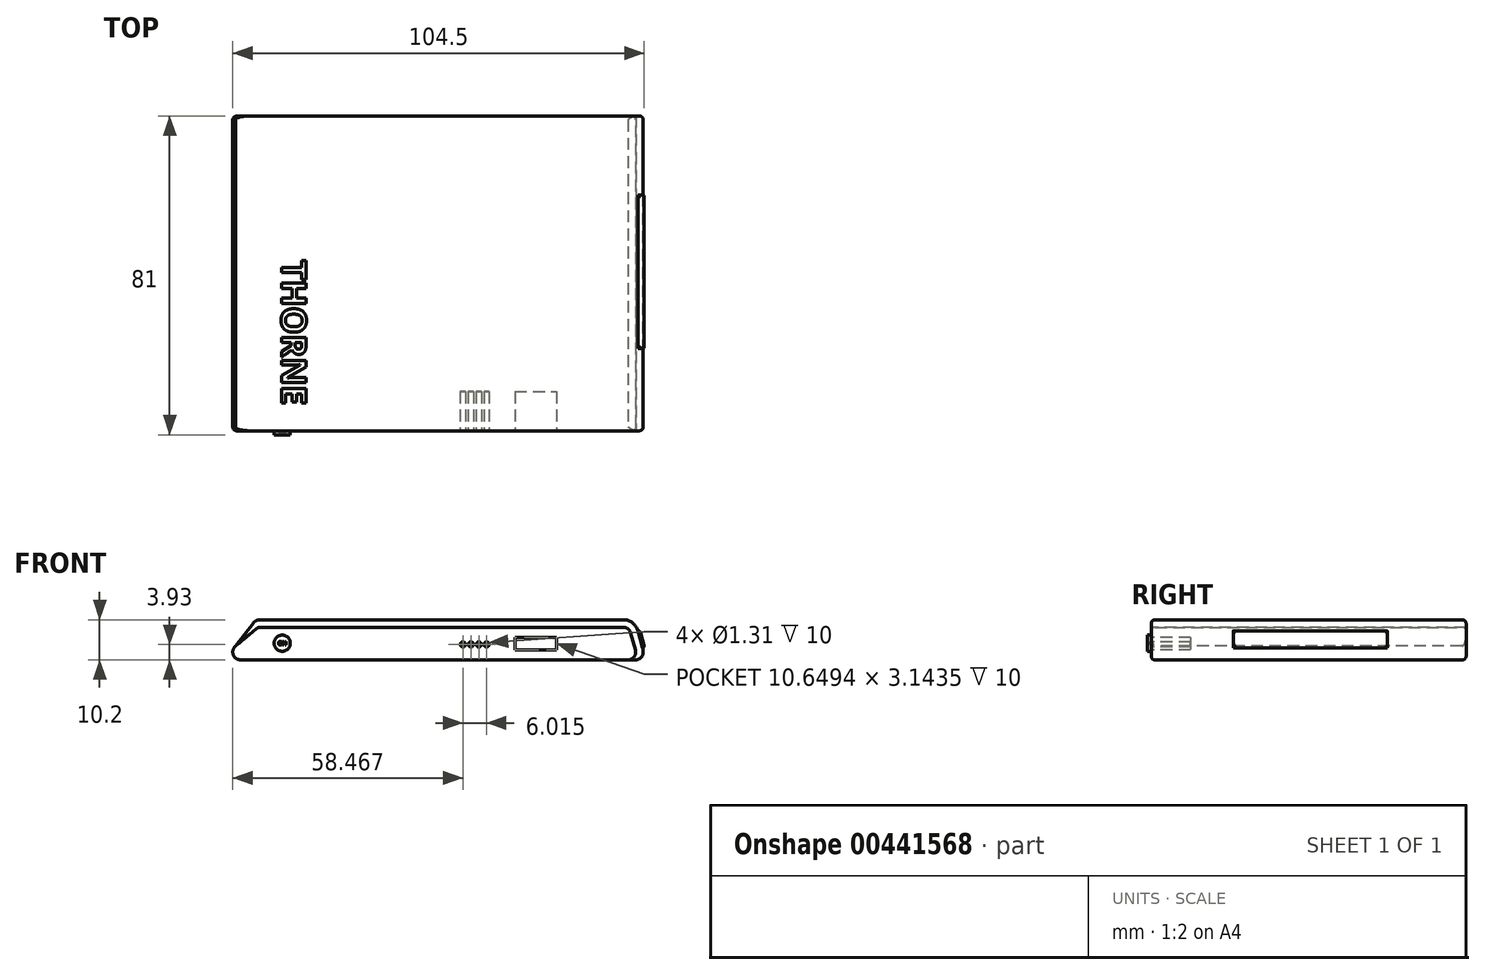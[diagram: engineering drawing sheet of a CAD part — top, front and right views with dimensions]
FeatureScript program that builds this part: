
annotation { "Feature Type Name" : "Feature", "Feature Type Description" : "" }
export const myFeature = defineFeature(function(context is Context, id is Id, definition is map)
    precondition{}
    {
        {
            var Q0;
            Q0=qCreatedBy(makeId("Front.planeOp"),FACE);
            var sketch = newSketch(context, id + "F0", { "sketchPlane" : qUnion([Q0])});
            skLineSegment(sketch, "E0", {"start": v(-44.25, -33) * mm, "end": v(54.14, -33) * mm});
            skFitSpline(sketch, "E1", {"points": [v(-49.78, -33) * mm, v(-39.82, -24.7) * mm], "startDerivative": vector(9.96, 8.3) * mm, "endDerivative": vector(9.96, 8.3) * mm});
            skLineSegment(sketch, "E2", {"start": v(-39.1, -24.7) * mm, "end": v(52.92, -24.7) * mm});
            skLineSegment(sketch, "E3", {"start": v(54.85, -26.16) * mm, "end": v(56.06, -30.46) * mm});
            skArc(sketch, "E4.filletArc", {"start": v(-39.1, -24.7) * mm, "mid": v(-39.78, -24.82) * mm, "end": v(-40.38, -25.17) * mm});
            skArc(sketch, "E5.filletArc", {"start": v(-45.53, -29.46) * mm, "mid": v(-46.13, -31.68) * mm, "end": v(-44.25, -33) * mm});
            skPoint(sketch, "E6.visualSharp", {"position": v(56.78, -33) * mm});
            skArc(sketch, "E6.filletArc", {"start": v(54.14, -33) * mm, "mid": v(55.73, -32.2) * mm, "end": v(56.06, -30.46) * mm});
            skPoint(sketch, "E7.visualSharp", {"position": v(54.44, -24.7) * mm});
            skArc(sketch, "E7.filletArc", {"start": v(54.85, -26.16) * mm, "mid": v(54.13, -25.1) * mm, "end": v(52.92, -24.7) * mm});
            skSolve(sketch);
        }
        {
            var Q0;
            Q0=makeQuery(id+"F0.imprint","IMPRINT",FACE,{"disambiguationData":[TD([[makeQuery(id+"F0.imprint","IMPRINT",EDGE,{"derivedFrom":sQuery(id+"F0.wireOp",EDGE,"E0")}),1.0]])]});
            extrude(context, id + "F1", {"entities" : qUnion([Q0]), "depth" : 80 * mm});
        }
        {
            var Q0;
            Q0=makeQuery(id+"F1.opExtrude","CAP_FACE",FACE,{"disambiguationData":[OSD([sQuery(id+"F0.wireOp",EDGE,"E0"),sQuery(id+"F0.wireOp",EDGE,"E1"),sQuery(id+"F0.wireOp",EDGE,"E2"),sQuery(id+"F0.wireOp",EDGE,"E3"),sQuery(id+"F0.wireOp",EDGE,"E4.filletArc"),sQuery(id+"F0.wireOp",EDGE,"E5.filletArc"),sQuery(id+"F0.wireOp",EDGE,"E6.filletArc"),sQuery(id+"F0.wireOp",EDGE,"E7.filletArc")])],"isStart":false});
            var sketch = newSketch(context, id + "F2", { "sketchPlane" : qUnion([Q0])});
            skCircle(sketch, "E8", {"center": v(18.23, -29.07) * mm, "radius": 0.66 * mm});
            skCircle(sketch, "E9", {"center": v(12.22, -29.07) * mm, "radius": 0.66 * mm});
            skCircle(sketch, "E10", {"center": v(16.26, -29.07) * mm, "radius": 0.66 * mm});
            skCircle(sketch, "E11", {"center": v(14.24, -29.07) * mm, "radius": 0.66 * mm});
            skLineSegment(sketch, "E12.bottom", {"start": v(25.42, -27.31) * mm, "end": v(36.07, -27.31) * mm});
            skLineSegment(sketch, "E12.top", {"start": v(25.42, -30.46) * mm, "end": v(36.07, -30.46) * mm});
            skLineSegment(sketch, "E12.left", {"start": v(25.42, -27.31) * mm, "end": v(25.42, -30.46) * mm});
            skLineSegment(sketch, "E12.right", {"start": v(36.07, -27.31) * mm, "end": v(36.07, -30.46) * mm});
            skSolve(sketch);
        }
        {
            var Q0;
            Q0 = qSketchRegion(id + "F2", true);
            extrude(context, id + "F3", {"entities" : qUnion([Q0]), "operationType" : NewBodyOperationType.REMOVE, "oppositeDirection" : true, "depth" : 10 * mm});
        }
        {
            var Q0;
            Q0=makeQuery(id+"F1.opExtrude","CAP_FACE",FACE,{"disambiguationData":[OSD([sQuery(id+"F0.wireOp",EDGE,"E0"),sQuery(id+"F0.wireOp",EDGE,"E1"),sQuery(id+"F0.wireOp",EDGE,"E2"),sQuery(id+"F0.wireOp",EDGE,"E3"),sQuery(id+"F0.wireOp",EDGE,"E4.filletArc"),sQuery(id+"F0.wireOp",EDGE,"E5.filletArc"),sQuery(id+"F0.wireOp",EDGE,"E6.filletArc"),sQuery(id+"F0.wireOp",EDGE,"E7.filletArc")])],"isStart":false});
            var sketch = newSketch(context, id + "F4", { "sketchPlane" : qUnion([Q0])});
            skCircle(sketch, "E13", {"center": v(-33.68, -28.76) * mm, "radius": 2.05 * mm});
            skSolve(sketch);
        }
        {
            var Q0;
            Q0=makeQuery(id+"F4.imprint","IMPRINT",FACE,{"disambiguationData":[TD([[makeQuery(id+"F4.imprint","IMPRINT",EDGE,{"derivedFrom":sQuery(id+"F4.wireOp",EDGE,"E13")}),1.0]])]});
            extrude(context, id + "F5", {"entities" : qUnion([Q0]), "operationType" : NewBodyOperationType.ADD, "depth" : 1 * mm});
        }
        {
            var Q0;
            Q0=makeQuery(id+"F5.opExtrude","CAP_FACE",FACE,{"disambiguationData":[OSD([sQuery(id+"F4.wireOp",EDGE,"E13")])],"isStart":false});
            var sketch = newSketch(context, id + "F6", { "sketchPlane" : qUnion([Q0])});
            skText(sketch, "E14", { "text": "ON", "fontName": "OpenSans-Bold.ttf"});
            const initialGuessF6  = {"E14": [-0.03474, -0.02925, 1, 0, 0.00097]};
            skSetInitialGuess(sketch, initialGuessF6);
            skSolve(sketch);
        }
        {
            var Q0;
            Q0 = qSketchRegion(id + "F6", true);
            extrude(context, id + "F7", {"entities" : qUnion([Q0]), "operationType" : NewBodyOperationType.REMOVE, "oppositeDirection" : true, "depth" : 0.3 * mm});
        }
        {
            var Q0;
            Q0=makeQuery(id+"F1.opExtrude","CAP_FACE",FACE,{"disambiguationData":[OSD([sQuery(id+"F0.wireOp",EDGE,"E0"),sQuery(id+"F0.wireOp",EDGE,"E1"),sQuery(id+"F0.wireOp",EDGE,"E2"),sQuery(id+"F0.wireOp",EDGE,"E3"),sQuery(id+"F0.wireOp",EDGE,"E4.filletArc"),sQuery(id+"F0.wireOp",EDGE,"E5.filletArc"),sQuery(id+"F0.wireOp",EDGE,"E6.filletArc"),sQuery(id+"F0.wireOp",EDGE,"E7.filletArc")])],"isStart":false});
            var sketch = newSketch(context, id + "F8", { "sketchPlane" : qUnion([Q0])});
            skLineSegment(sketch, "E15", {"start": v(54.14, -33) * mm, "end": v(56.04, -33) * mm});
            skArc(sketch, "E16.0", {"start": v(58.04, -31) * mm, "mid": v(58, -30.46) * mm, "end": v(57.9, -29.94) * mm});
            skLineSegment(sketch, "E16.1", {"start": v(56.68, -25.64) * mm, "end": v(57.9, -29.94) * mm});
            skArc(sketch, "E16.2", {"start": v(56.68, -25.64) * mm, "mid": v(55.28, -23.6) * mm, "end": v(52.92, -22.8) * mm});
            skPoint(sketch, "E17.visualSharp", {"position": v(57.49, -33) * mm});
            skArc(sketch, "E17.filletArc", {"start": v(56.04, -33) * mm, "mid": v(57.45, -32.41) * mm, "end": v(58.04, -31) * mm});
            skLineSegment(sketch, "E18", {"start": v(52.92, -22.8) * mm, "end": v(-39.4, -22.8) * mm});
            skLineSegment(sketch, "E19", {"start": v(-40.98, -23.58) * mm, "end": v(-45.53, -29.46) * mm});
            skPoint(sketch, "E20.endSnap0", {"position": v(-39.78, -24.82) * mm});
            skArc(sketch, "E21.0", {"start": v(54.14, -33) * mm, "mid": v(55.73, -32.2) * mm, "end": v(56.06, -30.46) * mm});
            skLineSegment(sketch, "E21.1", {"start": v(54.85, -26.16) * mm, "end": v(56.06, -30.46) * mm});
            skFitSpline(sketch, "E21.2", {"points": [v(-49.78, -33) * mm, v(-46.46, -30.23) * mm, v(-43.14, -27.47) * mm, v(-39.82, -24.7) * mm]});
            skArc(sketch, "E21.3", {"start": v(-39.1, -24.7) * mm, "mid": v(-39.78, -24.82) * mm, "end": v(-40.38, -25.17) * mm});
            skLineSegment(sketch, "E21.4", {"start": v(-39.1, -24.7) * mm, "end": v(52.92, -24.7) * mm});
            skArc(sketch, "E21.5", {"start": v(54.85, -26.16) * mm, "mid": v(54.13, -25.1) * mm, "end": v(52.92, -24.7) * mm});
            skPoint(sketch, "E22.visualSharp", {"position": v(-40.38, -22.8) * mm});
            skArc(sketch, "E22.filletArc", {"start": v(-39.4, -22.8) * mm, "mid": v(-40.28, -23) * mm, "end": v(-40.98, -23.58) * mm});
            skSolve(sketch);
        }
        {
            var Q0;
            Q0=makeQuery(id+"F8.imprint","IMPRINT",FACE,{"disambiguationData":[TD([[makeQuery(id+"F8.imprint","IMPRINT",EDGE,{"derivedFrom":sQuery(id+"F8.wireOp",EDGE,"E15")}),1.0]])]});
            extrude(context, id + "F9", {"entities" : qUnion([Q0]), "oppositeDirection" : true, "depth" : 80 * mm});
        }
        {
            var Q0;
            Q0=makeQuery(id+"F9.opExtrude","SWEPT_FACE",FACE,{"disambiguationData":[OSD([sQuery(id+"F8.wireOp",EDGE,"E16.1")])]});
            var sketch = newSketch(context, id + "F10", { "sketchPlane" : qUnion([Q0])});
            skLineSegment(sketch, "E23.bottom", {"start": v(-59.14, -40.1) * mm, "end": v(-20.04, -40.1) * mm});
            skLineSegment(sketch, "E23.top", {"start": v(-59.14, -44.56) * mm, "end": v(-20.04, -44.56) * mm});
            skLineSegment(sketch, "E23.left", {"start": v(-59.14, -40.1) * mm, "end": v(-59.14, -44.56) * mm});
            skLineSegment(sketch, "E23.right", {"start": v(-20.04, -40.1) * mm, "end": v(-20.04, -44.56) * mm});
            skSolve(sketch);
        }
        {
            var Q0;
            Q0=makeQuery(id+"F10.imprint","IMPRINT",FACE,{"disambiguationData":[TD([[makeQuery(id+"F10.imprint","IMPRINT",EDGE,{"derivedFrom":sQuery(id+"F10.wireOp",EDGE,"E23.bottom")}),1.0]])]});
            extrude(context, id + "F11", {"entities" : qUnion([Q0]), "operationType" : NewBodyOperationType.ADD, "depth" : 0.5 * mm});
        }
        {
            var Q0;
            Q0=makeQuery(id+"F11.opExtrude","CAP_FACE",FACE,{"disambiguationData":[OSD([sQuery(id+"F10.wireOp",EDGE,"E23.bottom"),sQuery(id+"F10.wireOp",EDGE,"E23.top"),sQuery(id+"F10.wireOp",EDGE,"E23.left"),sQuery(id+"F10.wireOp",EDGE,"E23.right")])],"isStart":false});
            fillet(context, id + "F12", {"entities" : qUnion([Q0]), "radius" : 0.5 * mm, "tangentPropagation" : true, "allowEdgeOverflow" : false});
        }
        {
            var Q0;
            Q0=makeQuery(id+"F9.opExtrude","SWEPT_FACE",FACE,{"disambiguationData":[OSD([sQuery(id+"F8.wireOp",EDGE,"E18")])]});
            fillet(context, id + "F13", {"entities" : qUnion([Q0]), "radius" : 1 * mm, "tangentPropagation" : true, "allowEdgeOverflow" : false});
        }
        {
            var Q0;
            Q0=makeQuery(id+"F1.opExtrude","SWEPT_FACE",FACE,{"disambiguationData":[OSD([sQuery(id+"F0.wireOp",EDGE,"E0")])]});
            fillet(context, id + "F14", {"entities" : qUnion([Q0]), "radius" : 1 * mm, "tangentPropagation" : true, "allowEdgeOverflow" : false});
        }
        {
            var Q0;
            Q0=makeQuery(id+"F9.opExtrude","SWEPT_FACE",FACE,{"disambiguationData":[OSD([sQuery(id+"F8.wireOp",EDGE,"E18")])]});
            var sketch = newSketch(context, id + "F15", { "sketchPlane" : qUnion([Q0])});
            skText(sketch, "E24", { "text": "THORNE", "fontName": "OpenSans-Bold.ttf"});
            const initialGuessF15  = {"E24": [-0.0339, -0.0366, 0, -1, 0.00635]};
            skSetInitialGuess(sketch, initialGuessF15);
            skSolve(sketch);
        }
        {
            var Q0;
            Q0 = qSketchRegion(id + "F15", true);
            extrude(context, id + "F16", {"entities" : qUnion([Q0]), "operationType" : NewBodyOperationType.REMOVE, "oppositeDirection" : true, "depth" : 0.2 * mm});
        }
    });
